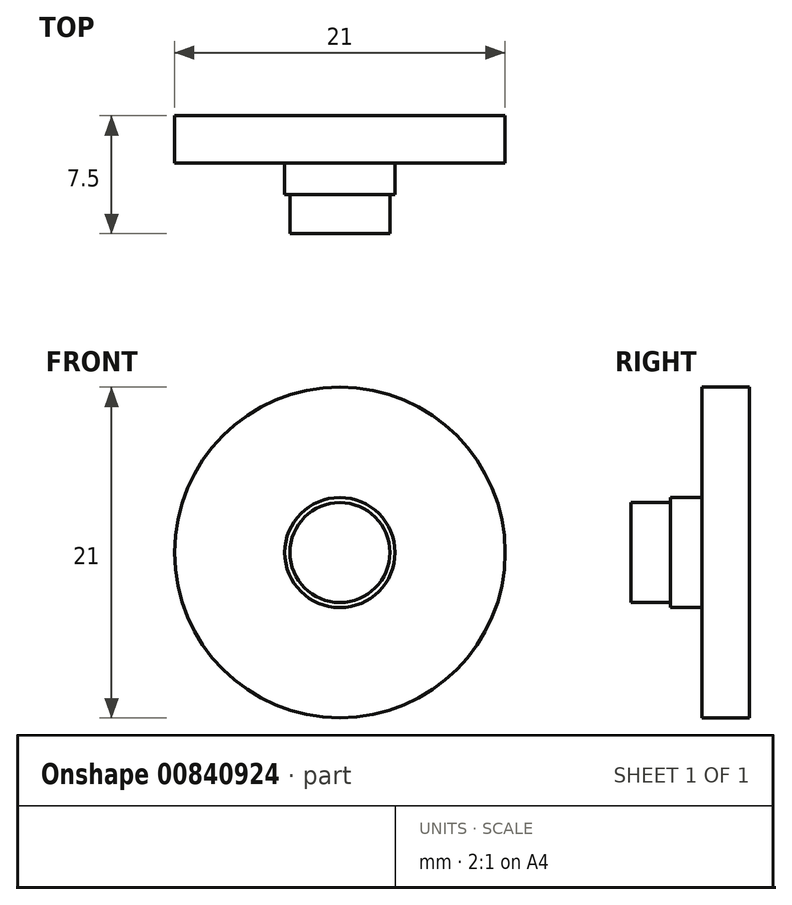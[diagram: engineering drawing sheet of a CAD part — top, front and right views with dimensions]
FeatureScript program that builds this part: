
annotation { "Feature Type Name" : "Feature", "Feature Type Description" : "" }
export const myFeature = defineFeature(function(context is Context, id is Id, definition is map)
    precondition{}
    {
        {
            var Q0;
            Q0=qCreatedBy(makeId("Front.planeOp"),FACE);
            var sketch = newSketch(context, id + "F0", { "sketchPlane" : qUnion([Q0])});
            skCircle(sketch, "E0", {"center": v(0, 0) * mm, "radius": 10.5 * mm});
            skSolve(sketch);
        }
        {
            var Q0;
            Q0=makeQuery(id+"F0.imprint","IMPRINT",FACE,{"disambiguationData":[TD([[makeQuery(id+"F0.imprint","IMPRINT",EDGE,{"derivedFrom":sQuery(id+"F0.wireOp",EDGE,"E0")}),1.0]])]});
            extrude(context, id + "F1", {"entities" : qUnion([Q0]), "depth" : 3 * mm, "offsetDistance" : 25 * mm});
        }
        {
            var Q0;
            Q0=makeQuery(id+"F1.opExtrude","CAP_FACE",FACE,{"disambiguationData":[OSD([sQuery(id+"F0.wireOp",EDGE,"E0")])],"isStart":false});
            var sketch = newSketch(context, id + "F2", { "sketchPlane" : qUnion([Q0])});
            skCircle(sketch, "E1", {"center": v(0, 0) * mm, "radius": 3.5 * mm});
            skSolve(sketch);
        }
        {
            var Q0;
            Q0=makeQuery(id+"F2.imprint","IMPRINT",FACE,{"disambiguationData":[TD([[makeQuery(id+"F2.imprint","IMPRINT",EDGE,{"derivedFrom":sQuery(id+"F2.wireOp",EDGE,"E1")}),1.0]])]});
            extrude(context, id + "F3", {"entities" : qUnion([Q0]), "operationType" : NewBodyOperationType.ADD, "depth" : 2 * mm, "offsetDistance" : 25 * mm});
        }
        {
            var Q0;
            Q0=makeQuery(id+"F3.opExtrude","CAP_FACE",FACE,{"disambiguationData":[OSD([sQuery(id+"F2.wireOp",EDGE,"E1")])],"isStart":false});
            var sketch = newSketch(context, id + "F4", { "sketchPlane" : qUnion([Q0])});
            skCircle(sketch, "E2", {"center": v(0, 0) * mm, "radius": 3.17 * mm});
            skSolve(sketch);
        }
        {
            var Q0;
            Q0=makeQuery(id+"F4.imprint","IMPRINT",FACE,{"disambiguationData":[TD([[makeQuery(id+"F4.imprint","IMPRINT",EDGE,{"derivedFrom":sQuery(id+"F4.wireOp",EDGE,"E2")}),1.0]])]});
            extrude(context, id + "F5", {"entities" : qUnion([Q0]), "operationType" : NewBodyOperationType.ADD, "depth" : 2.5 * mm, "offsetDistance" : 25 * mm});
        }
    });
